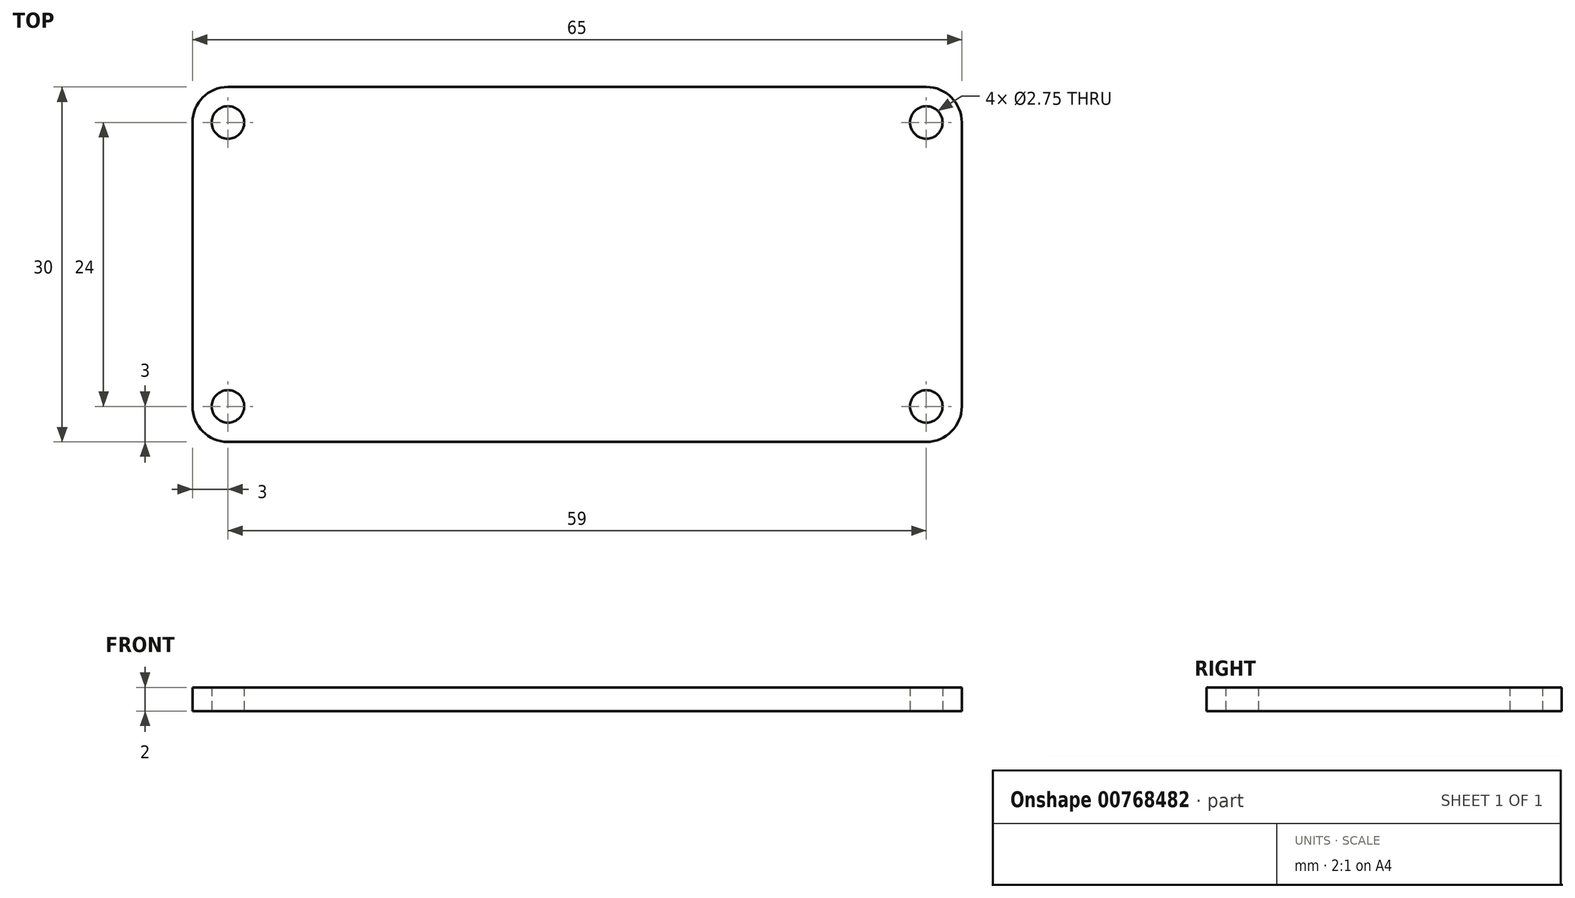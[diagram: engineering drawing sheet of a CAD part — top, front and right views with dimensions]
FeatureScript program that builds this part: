
annotation { "Feature Type Name" : "Feature", "Feature Type Description" : "" }
export const myFeature = defineFeature(function(context is Context, id is Id, definition is map)
    precondition{}
    {
        {
            var Q0;
            Q0=qCreatedBy(makeId("Top.planeOp"),FACE);
            var sketch = newSketch(context, id + "F0", { "sketchPlane" : qUnion([Q0])});
            skLineSegment(sketch, "E0.bottom", {"start": v(29.5, 15) * mm, "end": v(-29.5, 15) * mm});
            skLineSegment(sketch, "E0.top", {"start": v(29.5, -15) * mm, "end": v(-29.5, -15) * mm});
            skLineSegment(sketch, "E0.left", {"start": v(32.5, 12) * mm, "end": v(32.5, -12) * mm});
            skLineSegment(sketch, "E0.right", {"start": v(-32.5, 12) * mm, "end": v(-32.5, -12) * mm});
            skPoint(sketch, "E0.middle", {"position": v(0, 0) * mm});
            skPoint(sketch, "E1.visualSharp", {"position": v(-32.5, 15) * mm});
            skArc(sketch, "E1.filletArc", {"start": v(-29.5, 15) * mm, "mid": v(-31.62, 14.12) * mm, "end": v(-32.5, 12) * mm});
            skPoint(sketch, "E2.visualSharp", {"position": v(32.5, 15) * mm});
            skArc(sketch, "E2.filletArc", {"start": v(32.5, 12) * mm, "mid": v(31.62, 14.12) * mm, "end": v(29.5, 15) * mm});
            skPoint(sketch, "E3.visualSharp", {"position": v(32.5, -15) * mm});
            skArc(sketch, "E3.filletArc", {"start": v(29.5, -15) * mm, "mid": v(31.62, -14.12) * mm, "end": v(32.5, -12) * mm});
            skPoint(sketch, "E4.visualSharp", {"position": v(-32.5, -15) * mm});
            skArc(sketch, "E4.filletArc", {"start": v(-32.5, -12) * mm, "mid": v(-31.62, -14.12) * mm, "end": v(-29.5, -15) * mm});
            skCircle(sketch, "E5", {"center": v(-29.5, 12) * mm, "radius": 1.38 * mm});
            skLineSegment(sketch, "E6.bottom", {"start": v(-25, 9) * mm, "end": v(25, 9) * mm});
            skLineSegment(sketch, "E6.top", {"start": v(-25, 14) * mm, "end": v(25, 14) * mm});
            skLineSegment(sketch, "E6.left", {"start": v(-25, 9) * mm, "end": v(-25, 14) * mm});
            skLineSegment(sketch, "E6.right", {"start": v(25, 9) * mm, "end": v(25, 14) * mm});
            skPoint(sketch, "E6.middle", {"position": v(0, 11.5) * mm});
            skCircle(sketch, "E7.MirrorC", {"center": v(29.5, 12) * mm, "radius": 1.38 * mm});
            skCircle(sketch, "E8.MirrorC", {"center": v(-29.5, -12) * mm, "radius": 1.38 * mm});
            skCircle(sketch, "E9.MirrorC", {"center": v(29.5, -12) * mm, "radius": 1.38 * mm});
            skSolve(sketch);
        }
        {
            var Q0;
            Q0 = qSketchRegion(id + "F0", true);
            var Q1;
            Q1=makeQuery(id+"F0.imprint","IMPRINT",FACE,{"disambiguationData":[TD([[makeQuery(id+"F0.imprint","IMPRINT",EDGE,{"derivedFrom":sQuery(id+"F0.wireOp",EDGE,"E6.bottom")}),1.0]])]});
            extrude(context, id + "F1", {"entities" : qUnion([Q0, Q1]), "depth" : 2 * mm, "offsetDistance" : 25 * mm});
        }
    });
